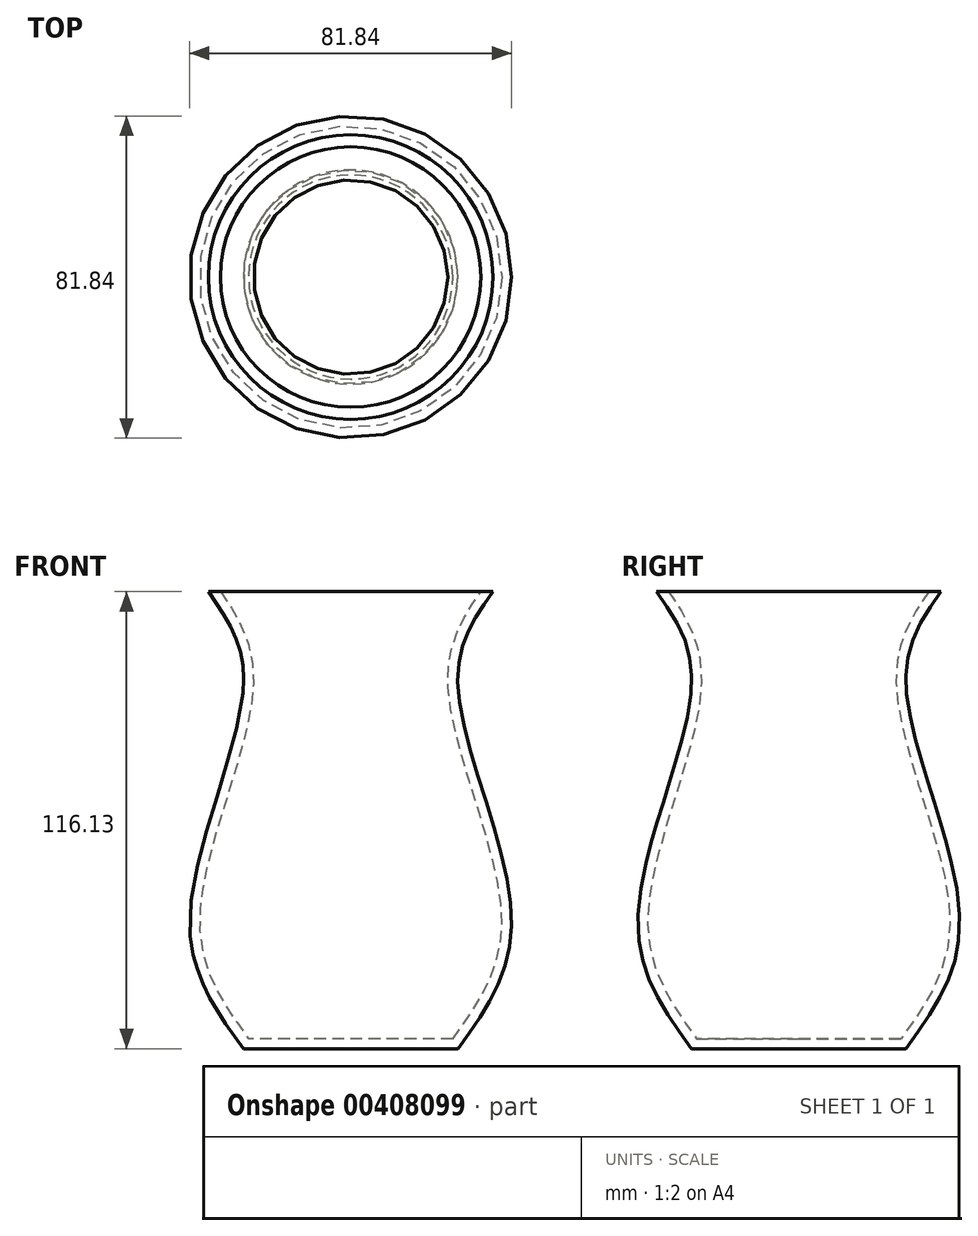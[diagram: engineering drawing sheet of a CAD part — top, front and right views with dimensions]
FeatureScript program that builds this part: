
annotation { "Feature Type Name" : "Feature", "Feature Type Description" : "" }
export const myFeature = defineFeature(function(context is Context, id is Id, definition is map)
    precondition{}
    {
        {
            var Q0;
            Q0=qCreatedBy(makeId("Front.planeOp"),FACE);
            var sketch = newSketch(context, id + "F0", { "sketchPlane" : qUnion([Q0])});
            skLineSegment(sketch, "E0", {"start": v(0, 0) * mm, "end": v(-27.2, 0) * mm});
            skFitSpline(sketch, "E1", {"points": [v(-27.2, 0) * mm, v(-40.9, 32.9) * mm, v(-27.2, 92.74) * mm, v(-36.15, 116.13) * mm], "startDerivative": vector(-65.97, 90.14) * mm, "endDerivative": vector(-52.37, 73.6) * mm});
            skLineSegment(sketch, "E2", {"start": v(-36.15, 116.13) * mm, "end": v(0, 116.13) * mm});
            skLineSegment(sketch, "E3", {"start": v(0, 116.13) * mm, "end": v(0, 0) * mm});
            skSolve(sketch);
        }
        {
            var Q0;
            Q0=makeQuery(id+"F0.imprint","IMPRINT",FACE,{"disambiguationData":[TD([[makeQuery(id+"F0.imprint","IMPRINT",EDGE,{"derivedFrom":sQuery(id+"F0.wireOp",EDGE,"E0")}),-1.0]])]});
            var Q1;
            Q1=sQuery(id+"F0.wireOp",EDGE,"E3");
            revolve(context, id + "F1", {"entities" : qUnion([Q0]), "axis" : qUnion([Q1]), "revolveType" : RevolveType.FULL});
        }
        {
            var Q0;
            Q0=makeQuery(id+"F1.opRevolve","SWEPT_FACE",FACE,{"disambiguationData":[OSD([sQuery(id+"F0.wireOp",EDGE,"E2")])]});
            shell(context, id + "F2", {"entities" : qUnion([Q0]), "thickness" : 2.5 * mm});
        }
    });
